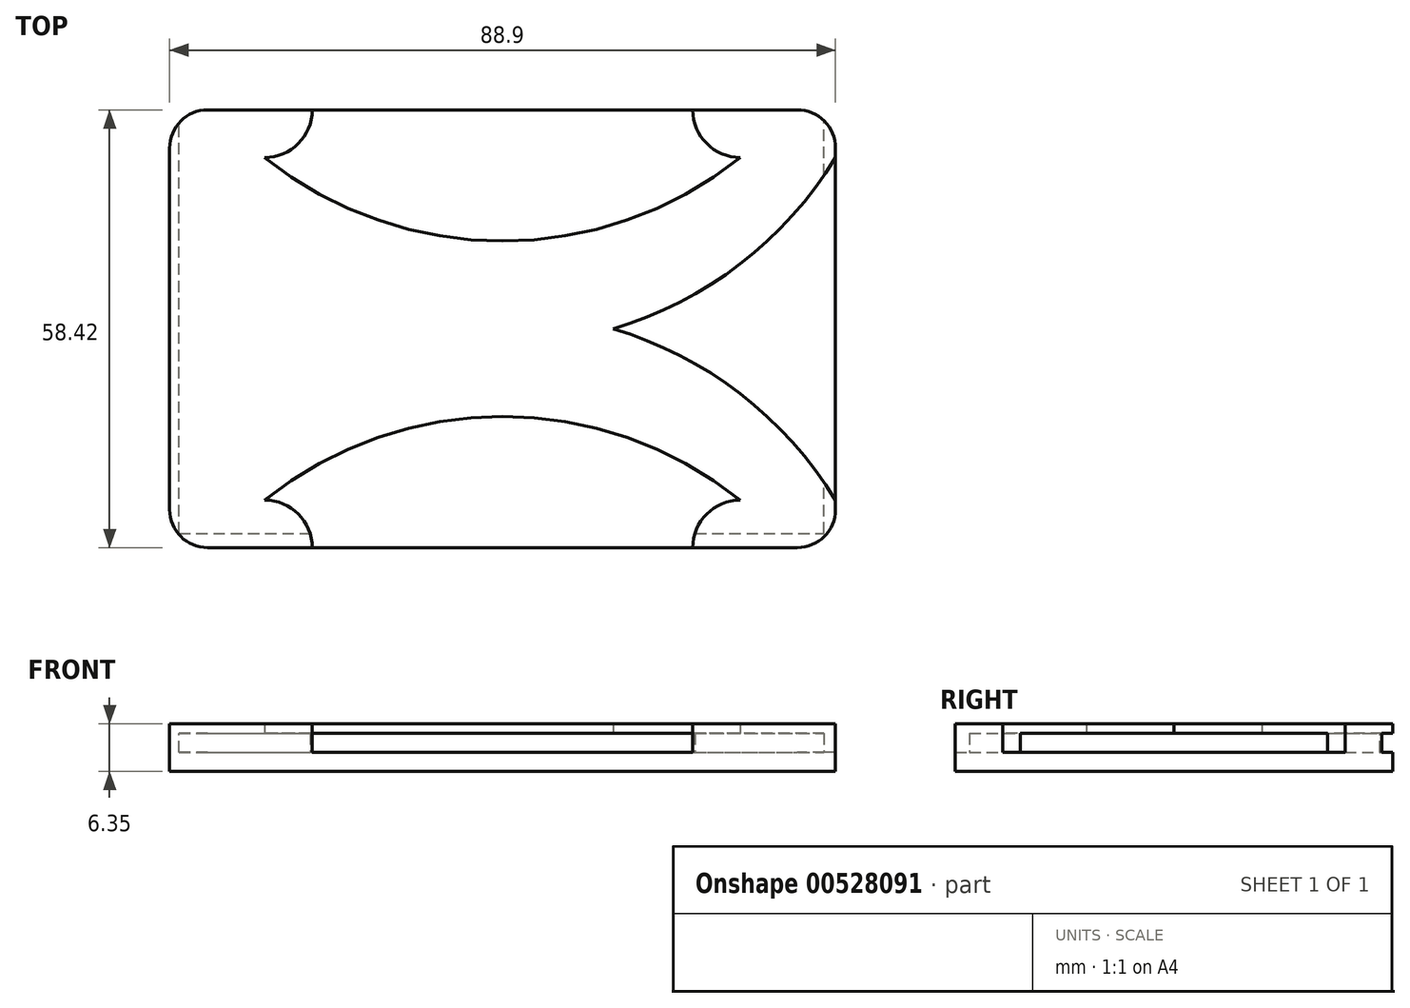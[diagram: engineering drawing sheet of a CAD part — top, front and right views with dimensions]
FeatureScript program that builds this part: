
annotation { "Feature Type Name" : "Feature", "Feature Type Description" : "" }
export const myFeature = defineFeature(function(context is Context, id is Id, definition is map)
    precondition{}
    {
        {
            var Q0;
            Q0=qCreatedBy(makeId("Top.planeOp"),FACE);
            var sketch = newSketch(context, id + "F0", { "sketchPlane" : qUnion([Q0])});
            skLineSegment(sketch, "E0.bottom", {"start": v(-60.39, 26.28) * mm, "end": v(28.51, 26.28) * mm});
            skLineSegment(sketch, "E0.top", {"start": v(-60.39, -32.14) * mm, "end": v(28.51, -32.14) * mm});
            skLineSegment(sketch, "E0.left", {"start": v(-60.39, 26.28) * mm, "end": v(-60.39, -32.14) * mm});
            skLineSegment(sketch, "E0.right", {"start": v(28.51, 26.28) * mm, "end": v(28.51, -32.14) * mm});
            skSolve(sketch);
        }
        {
            var Q0;
            Q0 = qSketchRegion(id + "F0", true);
            extrude(context, id + "F1", {"entities" : qUnion([Q0]), "depth" : 2.54 * mm, "offsetDistance" : 25.4 * mm});
        }
        {
            var Q0;
            Q0=makeQuery(id+"F1.opExtrude","SWEPT_EDGE",EDGE,{"disambiguationData":[OSD([sQuery(id+"F0.wireOp",EDGE,"E0.bottom"),sQuery(id+"F0.wireOp",EDGE,"E0.left")])]});
            var Q1;
            Q1=makeQuery(id+"F1.opExtrude","SWEPT_EDGE",EDGE,{"disambiguationData":[OSD([sQuery(id+"F0.wireOp",EDGE,"E0.top"),sQuery(id+"F0.wireOp",EDGE,"E0.left")])]});
            var Q2;
            Q2=makeQuery(id+"F1.opExtrude","SWEPT_EDGE",EDGE,{"disambiguationData":[OSD([sQuery(id+"F0.wireOp",EDGE,"E0.top"),sQuery(id+"F0.wireOp",EDGE,"E0.right")])]});
            var Q3;
            Q3=makeQuery(id+"F1.opExtrude","SWEPT_EDGE",EDGE,{"disambiguationData":[OSD([sQuery(id+"F0.wireOp",EDGE,"E0.bottom"),sQuery(id+"F0.wireOp",EDGE,"E0.right")])]});
            fillet(context, id + "F2", {"entities" : qUnion([Q0, Q1, Q2, Q3]), "radius" : 5.08 * mm, "tangentPropagation" : true, "allowEdgeOverflow" : false});
        }
        {
            var Q0;
            Q0=makeQuery(id+"F1.opExtrude","CAP_FACE",FACE,{"disambiguationData":[OSD([sQuery(id+"F0.wireOp",EDGE,"E0.bottom"),sQuery(id+"F0.wireOp",EDGE,"E0.top"),sQuery(id+"F0.wireOp",EDGE,"E0.left"),sQuery(id+"F0.wireOp",EDGE,"E0.right")])],"isStart":false});
            var sketch = newSketch(context, id + "F3", { "sketchPlane" : qUnion([Q0])});
            skLineSegment(sketch, "E1.0", {"start": v(-60.39, 21.2) * mm, "end": v(-60.39, -27.06) * mm});
            skLineSegment(sketch, "E2.0.0", {"start": v(-60.39, 21.2) * mm, "end": v(-60.39, 19.93) * mm});
            skArc(sketch, "E2.0.1", {"start": v(-60.39, -27.06) * mm, "mid": v(-58.9, -30.65) * mm, "end": v(-55.3, -32.14) * mm});
            skLineSegment(sketch, "E2.0.2", {"start": v(-55.3, -32.14) * mm, "end": v(-41.34, -32.14) * mm});
            skArc(sketch, "E2.0.3", {"start": v(23.43, -32.14) * mm, "mid": v(27.02, -30.65) * mm, "end": v(28.51, -27.06) * mm});
            skLineSegment(sketch, "E2.0.4", {"start": v(28.51, -27.06) * mm, "end": v(28.51, -25.79) * mm});
            skArc(sketch, "E2.0.5", {"start": v(28.51, 21.2) * mm, "mid": v(27.02, 24.8) * mm, "end": v(23.43, 26.28) * mm});
            skLineSegment(sketch, "E2.0.6", {"start": v(23.43, 26.28) * mm, "end": v(9.46, 26.28) * mm});
            skArc(sketch, "E2.0.7", {"start": v(-55.3, 26.28) * mm, "mid": v(-58.9, 24.8) * mm, "end": v(-60.39, 21.2) * mm});
            skLineSegment(sketch, "E3", {"start": v(-41.34, -32.14) * mm, "end": v(-41.34, -32.14) * mm});
            skLineSegment(sketch, "E4", {"start": v(9.46, -32.14) * mm, "end": v(9.46, -32.14) * mm});
            skLineSegment(sketch, "E5.trimOffspring", {"start": v(-41.34, 26.28) * mm, "end": v(-41.34, 26.28) * mm});
            skLineSegment(sketch, "E6.trimOffspring", {"start": v(9.46, -32.14) * mm, "end": v(23.43, -32.14) * mm});
            skLineSegment(sketch, "E7.trimOffspring", {"start": v(-41.34, 26.28) * mm, "end": v(-55.3, 26.28) * mm});
            skLineSegment(sketch, "E8.trimOffspring", {"start": v(9.46, 26.28) * mm, "end": v(9.46, 26.28) * mm});
            skLineSegment(sketch, "E9.trimOffspring", {"start": v(28.51, 19.93) * mm, "end": v(28.51, 21.2) * mm});
            skLineSegment(sketch, "E10.trimOffspring", {"start": v(-60.39, -25.79) * mm, "end": v(-60.39, -27.06) * mm});
            skPoint(sketch, "E11.visualSharp", {"position": v(-41.34, -25.79) * mm});
            skArc(sketch, "E11.filletArc", {"start": v(-41.34, -32.14) * mm, "mid": v(-43.2, -27.65) * mm, "end": v(-47.69, -25.79) * mm});
            skPoint(sketch, "E12.visualSharp", {"position": v(-41.34, 19.93) * mm});
            skArc(sketch, "E12.filletArc", {"start": v(-47.69, 19.93) * mm, "mid": v(-43.2, 21.8) * mm, "end": v(-41.34, 26.28) * mm});
            skPoint(sketch, "E13.visualSharp", {"position": v(9.46, 19.93) * mm});
            skArc(sketch, "E13.filletArc", {"start": v(9.46, 26.28) * mm, "mid": v(11.32, 21.8) * mm, "end": v(15.81, 19.93) * mm});
            skPoint(sketch, "E14.visualSharp", {"position": v(9.46, -25.79) * mm});
            skArc(sketch, "E14.filletArc", {"start": v(15.81, -25.79) * mm, "mid": v(11.32, -27.65) * mm, "end": v(9.46, -32.14) * mm});
            skArc(sketch, "E15", {"start": v(15.81, -25.79) * mm, "mid": v(-15.94, -14.64) * mm, "end": v(-47.69, -25.79) * mm});
            skArc(sketch, "E16", {"start": v(28.51, -25.79) * mm, "mid": v(15.8, -11.59) * mm, "end": v(-1.18, -2.93) * mm});
            skArc(sketch, "E17.MirrorCS", {"start": v(28.51, 19.93) * mm, "mid": v(15.8, 5.74) * mm, "end": v(-1.18, -2.93) * mm});
            skArc(sketch, "E18.MirrorCS", {"start": v(15.81, 19.93) * mm, "mid": v(-15.94, 8.79) * mm, "end": v(-47.69, 19.93) * mm});
            skArc(sketch, "E19.trimOffspring", {"start": v(-30.7, -2.93) * mm, "mid": v(-47.67, -11.59) * mm, "end": v(-60.39, -25.79) * mm});
            skArc(sketch, "E20.trimOffspring", {"start": v(-30.7, -2.93) * mm, "mid": v(-47.67, 5.74) * mm, "end": v(-60.39, 19.93) * mm});
            skSolve(sketch);
        }
        {
            var Q0;
            Q0 = qSketchRegion(id + "F3", true);
            extrude(context, id + "F4", {"entities" : qUnion([Q0]), "operationType" : NewBodyOperationType.ADD, "depth" : 3.8 * mm, "offsetDistance" : 25.4 * mm});
        }
        {
            var Q0;
            Q0=makeQuery(id+"F1.opExtrude","CAP_FACE",FACE,{"disambiguationData":[OSD([sQuery(id+"F0.wireOp",EDGE,"E0.bottom"),sQuery(id+"F0.wireOp",EDGE,"E0.top"),sQuery(id+"F0.wireOp",EDGE,"E0.left"),sQuery(id+"F0.wireOp",EDGE,"E0.right")])],"isStart":false});
            var sketch = newSketch(context, id + "F5", { "sketchPlane" : qUnion([Q0])});
            skLineSegment(sketch, "E21.bottom", {"start": v(-59.12, -30.23) * mm, "end": v(26.99, -30.23) * mm});
            skLineSegment(sketch, "E21.top", {"start": v(-59.12, 33.27) * mm, "end": v(26.99, 33.27) * mm});
            skLineSegment(sketch, "E21.left", {"start": v(-59.12, -30.23) * mm, "end": v(-59.12, 33.27) * mm});
            skLineSegment(sketch, "E21.right", {"start": v(26.99, -30.23) * mm, "end": v(26.99, 33.27) * mm});
            skSolve(sketch);
        }
        {
            var Q0;
            Q0 = qSketchRegion(id + "F5", true);
            extrude(context, id + "F6", {"entities" : qUnion([Q0]), "operationType" : NewBodyOperationType.REMOVE, "depth" : 2.54 * mm, "offsetDistance" : 25.4 * mm});
        }
    });
